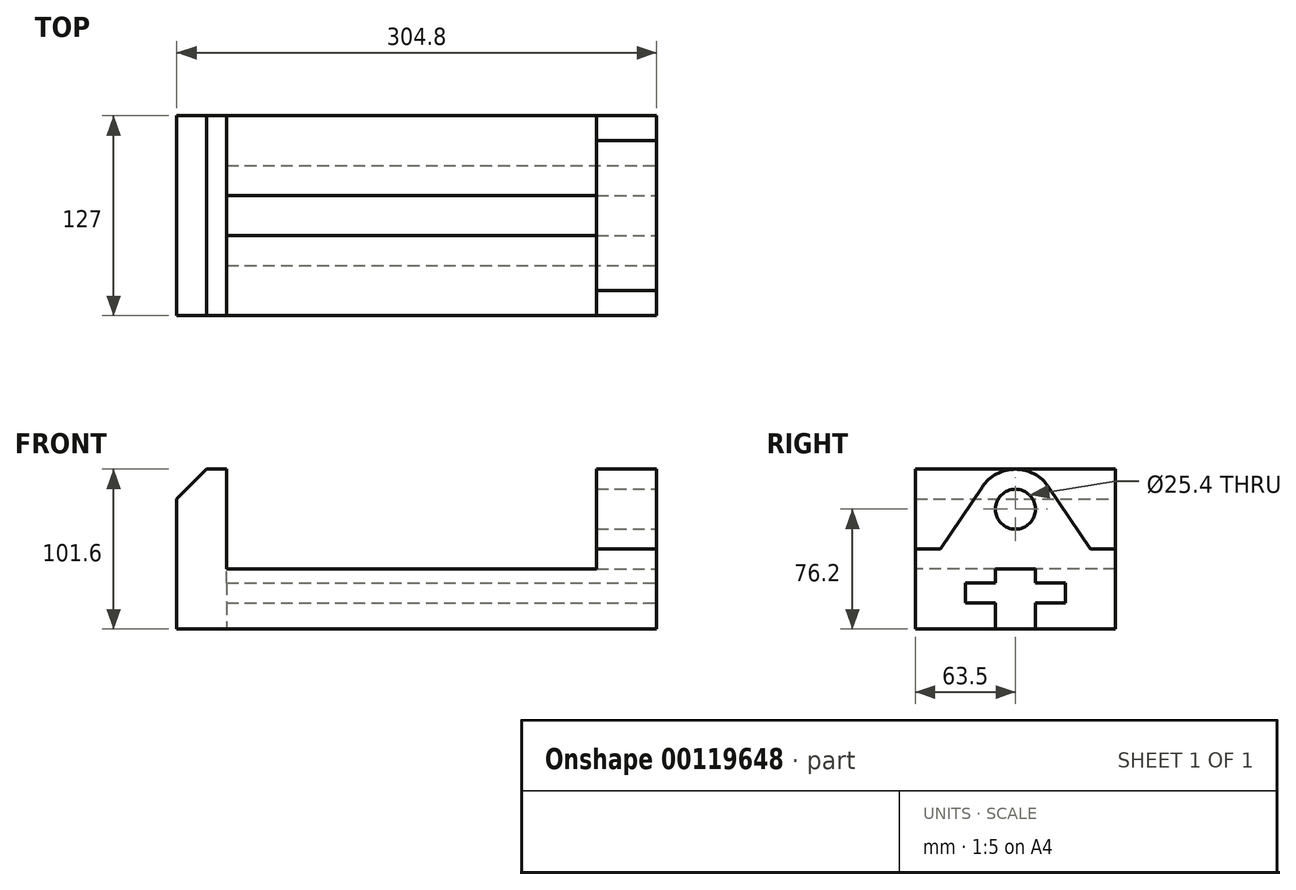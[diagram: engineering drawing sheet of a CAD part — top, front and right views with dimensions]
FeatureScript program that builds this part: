
annotation { "Feature Type Name" : "Feature", "Feature Type Description" : "" }
export const myFeature = defineFeature(function(context is Context, id is Id, definition is map)
    precondition{}
    {
        {
            var Q0;
            Q0=qCreatedBy(makeId("Right.planeOp"),FACE);
            var sketch = newSketch(context, id + "F0", { "sketchPlane" : qUnion([Q0])});
            skLineSegment(sketch, "E0.bottom", {"start": v(0, 0) * mm, "end": v(50.8, 0) * mm});
            skLineSegment(sketch, "E0.top", {"start": v(0, 50.8) * mm, "end": v(15.88, 50.8) * mm});
            skLineSegment(sketch, "E0.left", {"start": v(0, 0) * mm, "end": v(0, 50.8) * mm});
            skLineSegment(sketch, "E0.right", {"start": v(127, 0) * mm, "end": v(127, 50.8) * mm});
            skLineSegment(sketch, "E1", {"start": v(50.8, 0) * mm, "end": v(50.8, 16.5) * mm});
            skLineSegment(sketch, "E2", {"start": v(50.8, 16.5) * mm, "end": v(31.75, 16.5) * mm});
            skLineSegment(sketch, "E3", {"start": v(31.75, 16.5) * mm, "end": v(31.75, 29.2) * mm});
            skLineSegment(sketch, "E4", {"start": v(31.75, 29.21) * mm, "end": v(50.8, 29.21) * mm});
            skLineSegment(sketch, "E5", {"start": v(50.8, 29.21) * mm, "end": v(50.8, 38.1) * mm});
            skLineSegment(sketch, "E6", {"start": v(50.8, 38.1) * mm, "end": v(76.2, 38.1) * mm});
            skLineSegment(sketch, "E7", {"start": v(76.2, 38.1) * mm, "end": v(76.2, 29.21) * mm});
            skLineSegment(sketch, "E8", {"start": v(76.2, 29.21) * mm, "end": v(95.25, 29.21) * mm});
            skLineSegment(sketch, "E9", {"start": v(95.25, 29.21) * mm, "end": v(95.25, 16.51) * mm});
            skLineSegment(sketch, "E10", {"start": v(95.25, 16.51) * mm, "end": v(76.2, 16.51) * mm});
            skLineSegment(sketch, "E11", {"start": v(76.2, 16.51) * mm, "end": v(76.2, 0) * mm});
            skLineSegment(sketch, "E12.trimOffspring", {"start": v(76.2, 0) * mm, "end": v(127, 0) * mm});
            skLineSegment(sketch, "E13", {"start": v(15.88, 50.8) * mm, "end": v(42.4, 90.35) * mm});
            skLineSegment(sketch, "E14", {"start": v(111.13, 50.8) * mm, "end": v(84.6, 90.35) * mm});
            skArc(sketch, "E15", {"start": v(84.6, 90.35) * mm, "mid": v(63.5, 101.6) * mm, "end": v(42.4, 90.35) * mm});
            skLineSegment(sketch, "E16.trimOffspring", {"start": v(111.13, 50.8) * mm, "end": v(127, 50.8) * mm});
            skCircle(sketch, "E17", {"center": v(63.5, 76.2) * mm, "radius": 12.7 * mm});
            skLineSegment(sketch, "E18", {"start": v(0, 38.1) * mm, "end": v(127, 38.1) * mm});
            skPoint(sketch, "E18.endSnap0", {"position": v(63.5, 38.1) * mm});
            skSolve(sketch);
        }
        {
            var Q0;
            Q0 = qSketchRegion(id + "F0", true);
            extrude(context, id + "F1", {"entities" : qUnion([Q0]), "oppositeDirection" : true, "depth" : 38.1 * mm});
        }
        {
            var Q0;
            Q0=makeQuery(id+"F1.opExtrude","CAP_FACE",FACE,{"disambiguationData":[OSD([sQuery(id+"F0.wireOp",EDGE,"E0.bottom"),sQuery(id+"F0.wireOp",EDGE,"E0.top"),sQuery(id+"F0.wireOp",EDGE,"E0.left"),sQuery(id+"F0.wireOp",EDGE,"E0.right"),sQuery(id+"F0.wireOp",EDGE,"E1"),sQuery(id+"F0.wireOp",EDGE,"E2"),sQuery(id+"F0.wireOp",EDGE,"E3"),sQuery(id+"F0.wireOp",EDGE,"E4"),sQuery(id+"F0.wireOp",EDGE,"E5"),sQuery(id+"F0.wireOp",EDGE,"E7"),sQuery(id+"F0.wireOp",EDGE,"E8"),sQuery(id+"F0.wireOp",EDGE,"E9"),sQuery(id+"F0.wireOp",EDGE,"E10"),sQuery(id+"F0.wireOp",EDGE,"E11"),sQuery(id+"F0.wireOp",EDGE,"E12.trimOffspring"),sQuery(id+"F0.wireOp",EDGE,"E13"),sQuery(id+"F0.wireOp",EDGE,"E14"),sQuery(id+"F0.wireOp",EDGE,"E15"),sQuery(id+"F0.wireOp",EDGE,"E16.trimOffspring"),sQuery(id+"F0.wireOp",EDGE,"E17"),sQuery(id+"F0.wireOp",EDGE,"E18")])],"isStart":false});
            var sketch = newSketch(context, id + "F2", { "sketchPlane" : qUnion([Q0])});
            skLineSegment(sketch, "E19", {"start": v(-127, 38.1) * mm, "end": v(0, 38.1) * mm});
            skSolve(sketch);
        }
        {
            var Q0;
            {var subQ0=makeQuery(id+"F1.opExtrude","CAP_EDGE",EDGE,{"disambiguationData":[OSD([sQuery(id+"F0.wireOp",EDGE,"E0.bottom")])],"isStart":false});Q0=makeQuery(id+"F2.imprint","IMPRINT",FACE,{"disambiguationData":[TD([[makeQuery(id+"F2.imprint","IMPRINT",EDGE,{"derivedFrom":subQ0}),-1.0]])]});}
            var Q1;
            {var subQ0=makeQuery(id+"F1.opExtrude","CAP_EDGE",EDGE,{"disambiguationData":[OSD([sQuery(id+"F0.wireOp",EDGE,"E7")])],"isStart":false});Q1=makeQuery(id+"F2.imprint","IMPRINT",FACE,{"disambiguationData":[TD([[makeQuery(id+"F2.imprint","IMPRINT",EDGE,{"derivedFrom":subQ0}),-1.0]])]});}
            extrude(context, id + "F3", {"entities" : qUnion([Q0, Q1]), "operationType" : NewBodyOperationType.ADD, "depth" : 234.95 * mm});
        }
        {
            var Q0;
            Q0=makeQuery(id+"F3.opExtrude","CAP_FACE",FACE,{"disambiguationData":[OSD([sQuery(id+"F0.wireOp",EDGE,"E0.right"),sQuery(id+"F0.wireOp",EDGE,"E7"),sQuery(id+"F0.wireOp",EDGE,"E8"),sQuery(id+"F0.wireOp",EDGE,"E9"),sQuery(id+"F0.wireOp",EDGE,"E10"),sQuery(id+"F0.wireOp",EDGE,"E11"),sQuery(id+"F0.wireOp",EDGE,"E12.trimOffspring"),sQuery(id+"F2.wireOp",EDGE,"E19")])],"isStart":false});
            var sketch = newSketch(context, id + "F4", { "sketchPlane" : qUnion([Q0])});
            skLineSegment(sketch, "E20.bottom", {"start": v(-127, 0) * mm, "end": v(0, 0) * mm});
            skLineSegment(sketch, "E20.top", {"start": v(-127, 101.6) * mm, "end": v(0, 101.6) * mm});
            skLineSegment(sketch, "E20.left", {"start": v(-127, 0) * mm, "end": v(-127, 101.6) * mm});
            skLineSegment(sketch, "E20.right", {"start": v(0, 0) * mm, "end": v(0, 101.6) * mm});
            skSolve(sketch);
        }
        {
            var Q0;
            {var subQ4=sQuery(id+"F4.wireOp",EDGE,"E20.top");Q0=makeQuery(id+"F4.imprint","IMPRINT",FACE,{"disambiguationData":[TD([[makeQuery(id+"F4.imprint","IMPRINT",EDGE,{"derivedFrom":subQ4}),-1.0]])]});}
            var Q1;
            {var subQ0=sQuery(id+"F0.wireOp",EDGE,"E7");Q1=makeQuery(id+"F4.imprint","IMPRINT",FACE,{"disambiguationData":[TD([[makeQuery(id+"F4.imprint","IMPRINT",EDGE,{"derivedFrom":makeQuery(id+"F3.opExtrude","CAP_EDGE",EDGE,{"disambiguationData":[OSD([subQ0])],"isStart":false})}),-1.0]])]});}
            extrude(context, id + "F5", {"entities" : qUnion([Q0, Q1]), "operationType" : NewBodyOperationType.ADD, "depth" : 31.75 * mm});
        }
        {
            var Q0;
            Q0=makeQuery(id+"F5.opExtrude","CAP_EDGE",EDGE,{"disambiguationData":[OSD([sQuery(id+"F4.wireOp",EDGE,"E20.top")])],"isStart":false});
            chamfer(context, id + "F6", {"entities" : qUnion([Q0]), "width" : 19.05 * mm, "tangentPropagation" : true});
        }
    });
